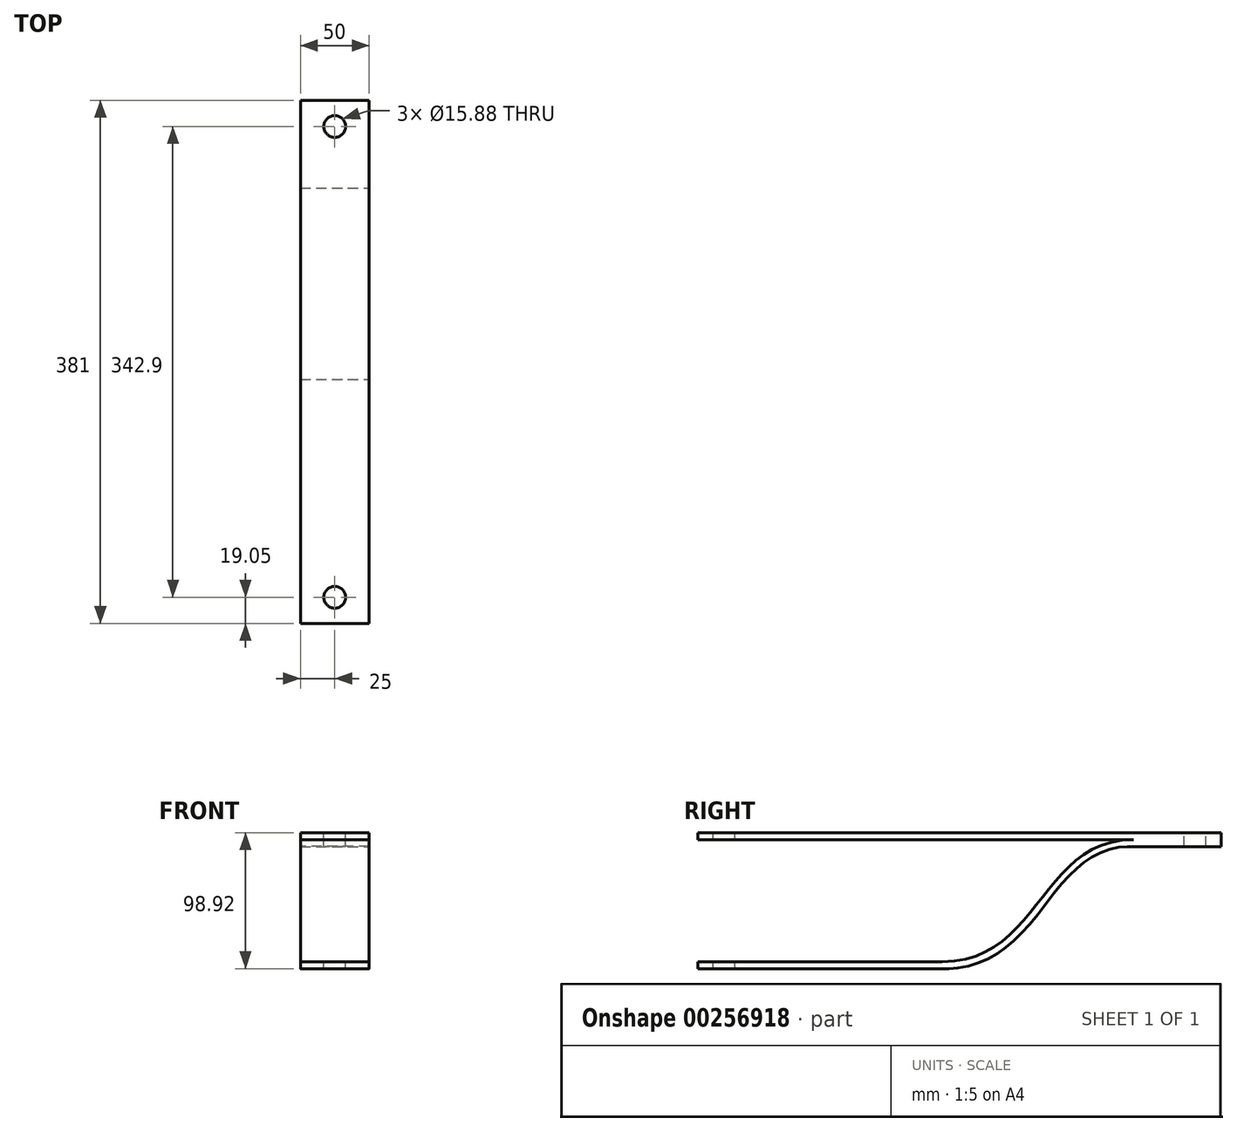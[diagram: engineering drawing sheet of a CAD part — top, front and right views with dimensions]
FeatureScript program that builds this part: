
annotation { "Feature Type Name" : "Feature", "Feature Type Description" : "" }
export const myFeature = defineFeature(function(context is Context, id is Id, definition is map)
    precondition{}
    {
        {
            var Q0;
            Q0=qCreatedBy(makeId("Right.planeOp"),FACE);
            var sketch = newSketch(context, id + "F0", { "sketchPlane" : qUnion([Q0])});
            skLineSegment(sketch, "E0.bottom", {"start": v(0, 0) * mm, "end": v(381, 0) * mm});
            skLineSegment(sketch, "E0.top", {"start": v(0, 5) * mm, "end": v(381, 5) * mm});
            skLineSegment(sketch, "E0.left", {"start": v(0, 0) * mm, "end": v(0, 5) * mm});
            skLineSegment(sketch, "E0.right", {"start": v(381, 0) * mm, "end": v(381, 5) * mm});
            skLineSegment(sketch, "E1", {"start": v(0, 0) * mm, "end": v(0, -88.9) * mm, "construction": true});
            skLineSegment(sketch, "E2.bottom", {"start": v(0, -88.9) * mm, "end": v(177.8, -88.9) * mm});
            skLineSegment(sketch, "E2.top", {"start": v(0, -93.9) * mm, "end": v(177.8, -93.9) * mm});
            skLineSegment(sketch, "E2.left", {"start": v(0, -88.9) * mm, "end": v(0, -93.9) * mm});
            skLineSegment(sketch, "E3.bottom", {"start": v(381, 0) * mm, "end": v(317.06, 0) * mm});
            skLineSegment(sketch, "E3.top", {"start": v(381, -5) * mm, "end": v(317.06, -5) * mm});
            skLineSegment(sketch, "E3.left", {"start": v(381, 0) * mm, "end": v(381, -5) * mm});
            skFitSpline(sketch, "E4", {"points": [v(177.8, -88.9) * mm, v(317.06, 0) * mm], "startDerivative": vector(213.54, 0) * mm, "endDerivative": vector(204.25, 0) * mm});
            skFitSpline(sketch, "E5.0", {"points": [v(177.8, -93.9) * mm, v(182.5, -93.9) * mm, v(191.4, -93.16) * mm, v(203.3, -90.08) * mm, v(213.86, -85.3) * mm, v(223.2, -79.17) * mm, v(231.5, -72.03) * mm, v(241.5, -61.56) * mm, v(252.61, -47.45) * mm, v(263.3, -33.75) * mm, v(272.35, -24.05) * mm, v(279.56, -17.65) * mm, v(287.37, -12.34) * mm, v(295.98, -8.28) * mm, v(305.68, -5.65) * mm, v(313.08, -5) * mm, v(317.06, -5) * mm]});
            skSolve(sketch);
        }
        {
            var Q0;
            Q0=makeQuery(id+"F0.imprint","IMPRINT",FACE,{"disambiguationData":[TD([[makeQuery(id+"F0.imprint","IMPRINT",EDGE,{"derivedFrom":sQuery(id+"F0.wireOp",EDGE,"E0.bottom")}),1.0]])]});
            var Q1;
            Q1=makeQuery(id+"F0.imprint","IMPRINT",FACE,{"disambiguationData":[TD([[makeQuery(id+"F0.imprint","IMPRINT",EDGE,{"derivedFrom":sQuery(id+"F0.wireOp",EDGE,"E2.bottom")}),-1.0]])]});
            extrude(context, id + "F1", {"entities" : qUnion([Q0, Q1]), "oppositeDirection" : true, "depth" : 50 * mm});
        }
        {
            var Q0;
            Q0=makeQuery(id+"F1.opExtrude","SWEPT_FACE",FACE,{"disambiguationData":[OSD([sQuery(id+"F0.wireOp",EDGE,"E0.top")])]});
            var sketch = newSketch(context, id + "F2", { "sketchPlane" : qUnion([Q0])});
            skCircle(sketch, "E6", {"center": v(-25, 19.05) * mm, "radius": 7.94 * mm});
            skPoint(sketch, "E6.centerSnap0", {"position": v(-25, 0) * mm});
            skCircle(sketch, "E7", {"center": v(-25, 361.95) * mm, "radius": 7.94 * mm});
            skPoint(sketch, "E7.centerSnap0", {"position": v(-25, 381) * mm});
            skSolve(sketch);
        }
        {
            var Q0;
            Q0=makeQuery(id+"F2.imprint","IMPRINT",FACE,{"disambiguationData":[TD([[makeQuery(id+"F2.imprint","IMPRINT",EDGE,{"derivedFrom":sQuery(id+"F2.wireOp",EDGE,"E7")}),1.0]])]});
            var Q1;
            Q1=makeQuery(id+"F2.imprint","IMPRINT",FACE,{"disambiguationData":[TD([[makeQuery(id+"F2.imprint","IMPRINT",EDGE,{"derivedFrom":sQuery(id+"F2.wireOp",EDGE,"E6")}),1.0]])]});
            extrude(context, id + "F3", {"entities" : qUnion([Q0, Q1]), "operationType" : NewBodyOperationType.REMOVE, "endBound" : BoundingType.THROUGH_ALL, "oppositeDirection" : true, "depth" : 25.4 * mm});
        }
    });
